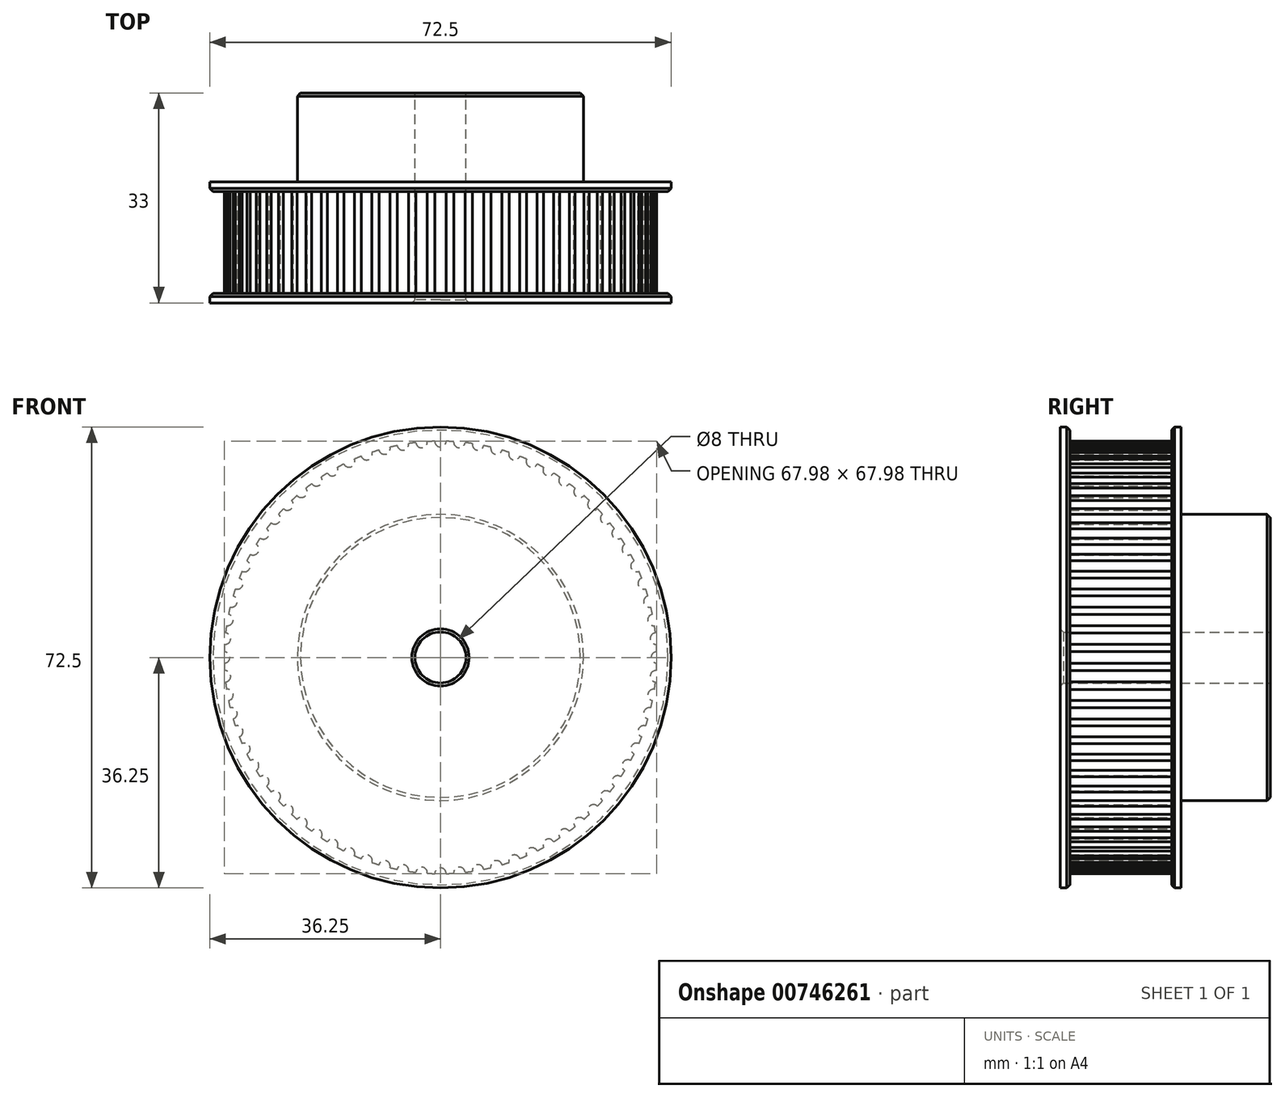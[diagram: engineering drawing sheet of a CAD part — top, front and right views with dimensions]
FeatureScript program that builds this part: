
annotation { "Feature Type Name" : "Feature", "Feature Type Description" : "" }
export const myFeature = defineFeature(function(context is Context, id is Id, definition is map)
    precondition{}
    {
        {
            var Q0;
            Q0=qCreatedBy(makeId("Front.planeOp"),FACE);
            var sketch = newSketch(context, id + "F0", { "sketchPlane" : qUnion([Q0])});
            skCircle(sketch, "E0", {"center": v(0, 0) * mm, "radius": 34 * mm});
            skSolve(sketch);
        }
        {
            var Q0;
            Q0=makeQuery(id+"F0.imprint","IMPRINT",FACE,{"disambiguationData":[TD([[makeQuery(id+"F0.imprint","IMPRINT",EDGE,{"derivedFrom":sQuery(id+"F0.wireOp",EDGE,"E0")}),1.0]])]});
            extrude(context, id + "F1", {"entities" : qUnion([Q0]), "endBound" : BoundingType.SYMMETRIC, "depth" : 16 * mm, "offsetDistance" : 25 * mm});
        }
        {
            var Q0;
            Q0=makeQuery(id+"F1.opExtrude","CAP_FACE",FACE,{"disambiguationData":[OSD([sQuery(id+"F0.wireOp",EDGE,"E0")])],"isStart":false});
            var sketch = newSketch(context, id + "F2", { "sketchPlane" : qUnion([Q0])});
            skCircle(sketch, "E1", {"center": v(0, 0) * mm, "radius": 36.25 * mm});
            skSolve(sketch);
        }
        {
            var Q0;
            Q0=qSketchRegion(id+"F2",true);
            extrude(context, id + "F3", {"entities" : qUnion([Q0]), "operationType" : NewBodyOperationType.ADD, "depth" : 1.5 * mm, "offsetDistance" : 25 * mm});
        }
        {
            var Q0;
            Q0=makeQuery(id+"F1.opExtrude","CAP_FACE",FACE,{"disambiguationData":[OSD([sQuery(id+"F0.wireOp",EDGE,"E0")])],"isStart":true});
            var sketch = newSketch(context, id + "F4", { "sketchPlane" : qUnion([Q0])});
            skCircle(sketch, "E2", {"center": v(0, 0) * mm, "radius": 36.25 * mm});
            skSolve(sketch);
        }
        {
            var Q0;
            Q0=qSketchRegion(id+"F4",true);
            extrude(context, id + "F5", {"entities" : qUnion([Q0]), "operationType" : NewBodyOperationType.ADD, "depth" : 1.5 * mm, "offsetDistance" : 25 * mm});
        }
        {
            var Q0;
            Q0=makeQuery(id+"F5.opExtrude","CAP_FACE",FACE,{"disambiguationData":[OSD([sQuery(id+"F4.wireOp",EDGE,"E2")])],"isStart":false});
            var sketch = newSketch(context, id + "F6", { "sketchPlane" : qUnion([Q0])});
            skCircle(sketch, "E3", {"center": v(0, 0) * mm, "radius": 22.5 * mm});
            skSolve(sketch);
        }
        {
            var Q0;
            Q0=qSketchRegion(id+"F6",true);
            extrude(context, id + "F7", {"entities" : qUnion([Q0]), "operationType" : NewBodyOperationType.ADD, "depth" : 14 * mm, "offsetDistance" : 25 * mm});
        }
        {
            var Q0;
            Q0=makeQuery(id+"F7.opExtrude","CAP_FACE",FACE,{"disambiguationData":[OSD([sQuery(id+"F6.wireOp",EDGE,"E3")])],"isStart":false});
            var sketch = newSketch(context, id + "F8", { "sketchPlane" : qUnion([Q0])});
            skCircle(sketch, "E4", {"center": v(0, 0) * mm, "radius": 4 * mm});
            skSolve(sketch);
        }
        {
            var Q0;
            Q0=qSketchRegion(id+"F8",true);
            extrude(context, id + "F9", {"entities" : qUnion([Q0]), "operationType" : NewBodyOperationType.REMOVE, "endBound" : BoundingType.THROUGH_ALL, "oppositeDirection" : true, "depth" : 25 * mm, "offsetDistance" : 25 * mm});
        }
        {
            var Q0;
            Q0=makeQuery(id+"F9.boolean.opBoolean","INTERSECT",EDGE,{"derivedFrom":[makeQuery(id+"F3.opExtrude","CAP_FACE",FACE,{"disambiguationData":[OSD([sQuery(id+"F2.wireOp",EDGE,"E1")])],"isStart":false}),makeQuery(id+"F9.opExtrude","SWEPT_FACE",FACE,{"disambiguationData":[OSD([sQuery(id+"F8.wireOp",EDGE,"E4")])]})]});
            var Q1;
            Q1=makeQuery(id+"F9.boolean.opBoolean","COPY",EDGE,{"derivedFrom":makeQuery(id+"F9.opExtrude","CAP_EDGE",EDGE,{"disambiguationData":[OSD([sQuery(id+"F8.wireOp",EDGE,"E4")])],"isStart":true})});
            var Q2;
            Q2=makeQuery(id+"F3.opExtrude","CAP_EDGE",EDGE,{"disambiguationData":[OSD([sQuery(id+"F2.wireOp",EDGE,"E1")])],"isStart":true});
            var Q3;
            Q3=makeQuery(id+"F5.opExtrude","CAP_EDGE",EDGE,{"disambiguationData":[OSD([sQuery(id+"F4.wireOp",EDGE,"E2")])],"isStart":true});
            var Q4;
            Q4=makeQuery(id+"F7.opExtrude","CAP_EDGE",EDGE,{"disambiguationData":[OSD([sQuery(id+"F6.wireOp",EDGE,"E3")])],"isStart":false});
            chamfer(context, id + "F10", {"entities" : qUnion([Q0, Q1, Q2, Q3, Q4]), "width" : 0.5 * mm, "tangentPropagation" : true});
        }
        {
            var Q0;
            Q0=makeQuery(id+"F5.opExtrude","CAP_FACE",FACE,{"disambiguationData":[OSD([sQuery(id+"F4.wireOp",EDGE,"E2")])],"isStart":true});
            var sketch = newSketch(context, id + "F11", { "sketchPlane" : qUnion([Q0])});
            skCircle(sketch, "E5", {"center": v(0, 0) * mm, "radius": 38.86 * mm, "construction": true});
            skLineSegment(sketch, "E6", {"start": v(0, 0) * mm, "end": v(0, -34) * mm, "construction": true});
            skCircle(sketch, "E7", {"center": v(0, -34) * mm, "radius": 0.9 * mm});
            skCircle(sketch, "E8.1.0", {"center": v(2.96, -33.87) * mm, "radius": 0.9 * mm});
            skCircle(sketch, "E8.2.0", {"center": v(5.9, -33.48) * mm, "radius": 0.9 * mm});
            skCircle(sketch, "E8.3.0", {"center": v(8.8, -32.84) * mm, "radius": 0.9 * mm});
            skCircle(sketch, "E8.4.0", {"center": v(11.63, -31.95) * mm, "radius": 0.9 * mm});
            skCircle(sketch, "E8.5.0", {"center": v(14.37, -30.81) * mm, "radius": 0.9 * mm});
            skCircle(sketch, "E8.6.0", {"center": v(17, -29.44) * mm, "radius": 0.9 * mm});
            skCircle(sketch, "E8.7.0", {"center": v(19.5, -27.85) * mm, "radius": 0.9 * mm});
            skCircle(sketch, "E8.8.0", {"center": v(21.85, -26.05) * mm, "radius": 0.9 * mm});
            skCircle(sketch, "E8.9.0", {"center": v(24.04, -24.04) * mm, "radius": 0.9 * mm});
            skCircle(sketch, "E8.10.0", {"center": v(26.05, -21.85) * mm, "radius": 0.9 * mm});
            skCircle(sketch, "E8.11.0", {"center": v(27.85, -19.5) * mm, "radius": 0.9 * mm});
            skCircle(sketch, "E8.12.0", {"center": v(29.44, -17) * mm, "radius": 0.9 * mm});
            skCircle(sketch, "E8.13.0", {"center": v(30.81, -14.37) * mm, "radius": 0.9 * mm});
            skCircle(sketch, "E8.14.0", {"center": v(31.95, -11.63) * mm, "radius": 0.9 * mm});
            skCircle(sketch, "E8.15.0", {"center": v(32.84, -8.8) * mm, "radius": 0.9 * mm});
            skCircle(sketch, "E8.16.0", {"center": v(33.48, -5.9) * mm, "radius": 0.9 * mm});
            skCircle(sketch, "E8.17.0", {"center": v(33.87, -2.96) * mm, "radius": 0.9 * mm});
            skCircle(sketch, "E8.18.0", {"center": v(34, 0) * mm, "radius": 0.9 * mm});
            skCircle(sketch, "E8.19.0", {"center": v(33.87, 2.96) * mm, "radius": 0.9 * mm});
            skCircle(sketch, "E8.20.0", {"center": v(33.48, 5.9) * mm, "radius": 0.9 * mm});
            skCircle(sketch, "E8.21.0", {"center": v(32.84, 8.8) * mm, "radius": 0.9 * mm});
            skCircle(sketch, "E8.22.0", {"center": v(31.95, 11.63) * mm, "radius": 0.9 * mm});
            skCircle(sketch, "E8.23.0", {"center": v(30.81, 14.37) * mm, "radius": 0.9 * mm});
            skCircle(sketch, "E8.24.0", {"center": v(29.44, 17) * mm, "radius": 0.9 * mm});
            skCircle(sketch, "E8.25.0", {"center": v(27.85, 19.5) * mm, "radius": 0.9 * mm});
            skCircle(sketch, "E8.26.0", {"center": v(26.05, 21.85) * mm, "radius": 0.9 * mm});
            skCircle(sketch, "E8.27.0", {"center": v(24.04, 24.04) * mm, "radius": 0.9 * mm});
            skCircle(sketch, "E8.28.0", {"center": v(21.85, 26.05) * mm, "radius": 0.9 * mm});
            skCircle(sketch, "E8.29.0", {"center": v(19.5, 27.85) * mm, "radius": 0.9 * mm});
            skCircle(sketch, "E8.30.0", {"center": v(17, 29.44) * mm, "radius": 0.9 * mm});
            skCircle(sketch, "E8.31.0", {"center": v(14.37, 30.81) * mm, "radius": 0.9 * mm});
            skCircle(sketch, "E8.32.0", {"center": v(11.63, 31.95) * mm, "radius": 0.9 * mm});
            skCircle(sketch, "E8.33.0", {"center": v(8.8, 32.84) * mm, "radius": 0.9 * mm});
            skCircle(sketch, "E8.34.0", {"center": v(5.9, 33.48) * mm, "radius": 0.9 * mm});
            skCircle(sketch, "E8.35.0", {"center": v(2.96, 33.87) * mm, "radius": 0.9 * mm});
            skCircle(sketch, "E8.36.0", {"center": v(0, 34) * mm, "radius": 0.9 * mm});
            skCircle(sketch, "E8.37.0", {"center": v(-2.96, 33.87) * mm, "radius": 0.9 * mm});
            skCircle(sketch, "E8.38.0", {"center": v(-5.9, 33.48) * mm, "radius": 0.9 * mm});
            skCircle(sketch, "E8.39.0", {"center": v(-8.8, 32.84) * mm, "radius": 0.9 * mm});
            skCircle(sketch, "E8.40.0", {"center": v(-11.63, 31.95) * mm, "radius": 0.9 * mm});
            skCircle(sketch, "E8.41.0", {"center": v(-14.37, 30.81) * mm, "radius": 0.9 * mm});
            skCircle(sketch, "E8.42.0", {"center": v(-17, 29.44) * mm, "radius": 0.9 * mm});
            skCircle(sketch, "E8.43.0", {"center": v(-19.5, 27.85) * mm, "radius": 0.9 * mm});
            skCircle(sketch, "E8.44.0", {"center": v(-21.85, 26.05) * mm, "radius": 0.9 * mm});
            skCircle(sketch, "E8.45.0", {"center": v(-24.04, 24.04) * mm, "radius": 0.9 * mm});
            skCircle(sketch, "E8.46.0", {"center": v(-26.05, 21.85) * mm, "radius": 0.9 * mm});
            skCircle(sketch, "E8.47.0", {"center": v(-27.85, 19.5) * mm, "radius": 0.9 * mm});
            skCircle(sketch, "E8.48.0", {"center": v(-29.44, 17) * mm, "radius": 0.9 * mm});
            skCircle(sketch, "E8.49.0", {"center": v(-30.81, 14.37) * mm, "radius": 0.9 * mm});
            skCircle(sketch, "E8.50.0", {"center": v(-31.95, 11.63) * mm, "radius": 0.9 * mm});
            skCircle(sketch, "E8.51.0", {"center": v(-32.84, 8.8) * mm, "radius": 0.9 * mm});
            skCircle(sketch, "E8.52.0", {"center": v(-33.48, 5.9) * mm, "radius": 0.9 * mm});
            skCircle(sketch, "E8.53.0", {"center": v(-33.87, 2.96) * mm, "radius": 0.9 * mm});
            skCircle(sketch, "E8.54.0", {"center": v(-34, 0) * mm, "radius": 0.9 * mm});
            skCircle(sketch, "E8.55.0", {"center": v(-33.87, -2.96) * mm, "radius": 0.9 * mm});
            skCircle(sketch, "E8.56.0", {"center": v(-33.48, -5.9) * mm, "radius": 0.9 * mm});
            skCircle(sketch, "E8.57.0", {"center": v(-32.84, -8.8) * mm, "radius": 0.9 * mm});
            skCircle(sketch, "E8.58.0", {"center": v(-31.95, -11.63) * mm, "radius": 0.9 * mm});
            skCircle(sketch, "E8.59.0", {"center": v(-30.81, -14.37) * mm, "radius": 0.9 * mm});
            skCircle(sketch, "E8.60.0", {"center": v(-29.44, -17) * mm, "radius": 0.9 * mm});
            skCircle(sketch, "E8.61.0", {"center": v(-27.85, -19.5) * mm, "radius": 0.9 * mm});
            skCircle(sketch, "E8.62.0", {"center": v(-26.05, -21.85) * mm, "radius": 0.9 * mm});
            skCircle(sketch, "E8.63.0", {"center": v(-24.04, -24.04) * mm, "radius": 0.9 * mm});
            skCircle(sketch, "E8.64.0", {"center": v(-21.85, -26.05) * mm, "radius": 0.9 * mm});
            skCircle(sketch, "E8.65.0", {"center": v(-19.5, -27.85) * mm, "radius": 0.9 * mm});
            skCircle(sketch, "E8.66.0", {"center": v(-17, -29.44) * mm, "radius": 0.9 * mm});
            skCircle(sketch, "E8.67.0", {"center": v(-14.37, -30.81) * mm, "radius": 0.9 * mm});
            skCircle(sketch, "E8.68.0", {"center": v(-11.63, -31.95) * mm, "radius": 0.9 * mm});
            skCircle(sketch, "E8.69.0", {"center": v(-8.8, -32.84) * mm, "radius": 0.9 * mm});
            skCircle(sketch, "E8.70.0", {"center": v(-5.9, -33.48) * mm, "radius": 0.9 * mm});
            skCircle(sketch, "E8.71.0", {"center": v(-2.96, -33.87) * mm, "radius": 0.9 * mm});
            skSolve(sketch);
        }
        {
            var Q0;
            Q0=qSketchRegion(id+"F11",true);
            var Q1;
            Q1=makeQuery(id+"F3.opExtrude","CAP_FACE",FACE,{"disambiguationData":[OSD([sQuery(id+"F2.wireOp",EDGE,"E1")])],"isStart":true});
            extrude(context, id + "F12", {"entities" : qUnion([Q0]), "operationType" : NewBodyOperationType.REMOVE, "endBound" : BoundingType.UP_TO_SURFACE, "depth" : 25 * mm, "endBoundEntityFace" : qUnion([Q1]), "offsetDistance" : 25 * mm});
        }
    });
